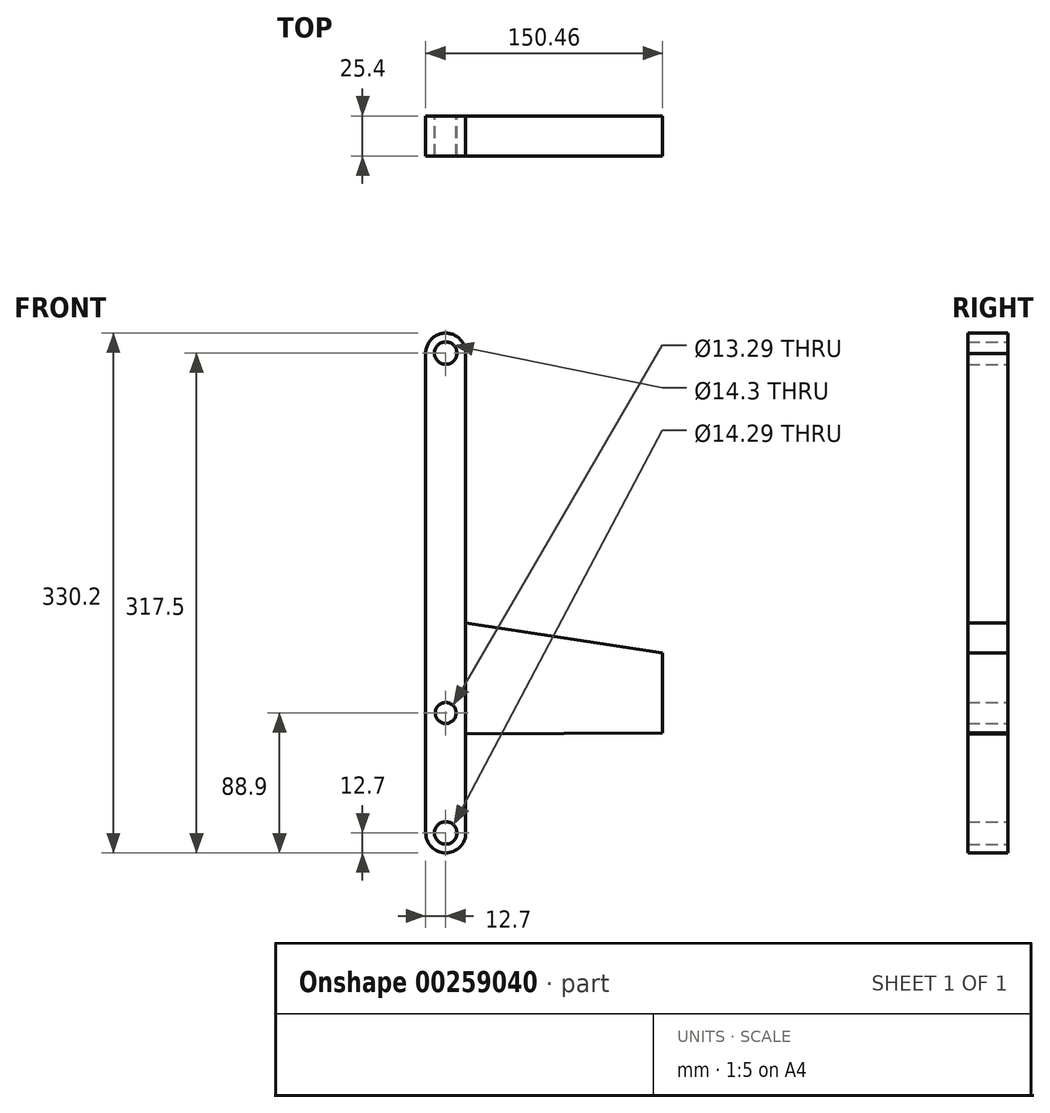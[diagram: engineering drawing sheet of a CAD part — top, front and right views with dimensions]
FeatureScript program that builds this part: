
annotation { "Feature Type Name" : "Feature", "Feature Type Description" : "" }
export const myFeature = defineFeature(function(context is Context, id is Id, definition is map)
    precondition{}
    {
        {
            var Q0;
            Q0=qCreatedBy(makeId("Front.planeOp"),FACE);
            var sketch = newSketch(context, id + "F0", { "sketchPlane" : qUnion([Q0])});
            skCircle(sketch, "E0", {"center": v(0, 0) * mm, "radius": 12.7 * mm});
            skCircle(sketch, "E1", {"center": v(0, 0) * mm, "radius": 7.15 * mm});
            skCircle(sketch, "E2", {"center": v(0, -304.8) * mm, "radius": 12.7 * mm});
            skCircle(sketch, "E3", {"center": v(0, -304.8) * mm, "radius": 7.15 * mm});
            skLineSegment(sketch, "E4", {"start": v(-12.7, 0) * mm, "end": v(-12.7, -304.8) * mm});
            skLineSegment(sketch, "E5", {"start": v(12.7, -0.45) * mm, "end": v(12.7, -304.8) * mm});
            skLineSegment(sketch, "E6.left", {"start": v(12.7, -228.19) * mm, "end": v(12.7, -266.29) * mm});
            skCircle(sketch, "E7", {"center": v(0, -228.6) * mm, "radius": 6.65 * mm});
            skLineSegment(sketch, "E8", {"start": v(12.7, -171.35) * mm, "end": v(137.55, -190.5) * mm});
            skLineSegment(sketch, "E9", {"start": v(137.55, -190.5) * mm, "end": v(137.76, -241.3) * mm});
            skLineSegment(sketch, "E10", {"start": v(137.76, -241.3) * mm, "end": v(12.7, -241.8) * mm});
            skLineSegment(sketch, "E11.MirrorCS", {"start": v(12.7, 0) * mm, "end": v(12.7, -304.8) * mm});
            skSolve(sketch);
        }
        {
            var Q0;
            {var subQ5=sQuery(id+"F0.wireOp",EDGE,"ePRVnAhi-Mh69-9U2p-dATt-yoKc0DpGRvop");Q0=makeQuery(id+"F0.imprint","IMPRINT",FACE,{"disambiguationData":[TD([[makeQuery(id+"F0.imprint","IMPRINT",EDGE,{"derivedFrom":subQ5}),-1.0]])]});}
            var Q1;
            Q1=makeQuery(id+"F0.imprint","IMPRINT",FACE,{"disambiguationData":[TD([[makeQuery(id+"F0.imprint","IMPRINT",EDGE,{"derivedFrom":sQuery(id+"F0.wireOp",EDGE,"E3")}),-1.0]])]});
            var Q2;
            {var subQ4=sQuery(id+"F0.wireOp",EDGE,"E4");Q2=makeQuery(id+"F0.imprint","IMPRINT",FACE,{"disambiguationData":[TD([[makeQuery(id+"F0.imprint","IMPRINT",EDGE,{"derivedFrom":subQ4}),1.0]])]});}
            var Q3;
            Q3=makeQuery(id+"F0.imprint","IMPRINT",FACE,{"disambiguationData":[TD([[makeQuery(id+"F0.imprint","IMPRINT",EDGE,{"derivedFrom":sQuery(id+"F0.wireOp",EDGE,"E1")}),-1.0]])]});
            var Q4;
            {var subQ0=sQuery(id+"F0.wireOp",EDGE,"E8");Q4=makeQuery(id+"F0.imprint","IMPRINT",FACE,{"disambiguationData":[TD([[makeQuery(id+"F0.imprint","IMPRINT",EDGE,{"derivedFrom":subQ0}),-1.0]])]});}
            var Q5;
            {var subQ0=sQuery(id+"F0.wireOp",EDGE,"yVrAon6F-TEJm-yE95-WjNk-o4wYu1XNi6pe");Q5=makeQuery(id+"F0.imprint","IMPRINT",FACE,{"disambiguationData":[TD([[makeQuery(id+"F0.imprint","IMPRINT",EDGE,{"derivedFrom":subQ0}),1.0]])]});}
            var Q6;
            {var subQ0=sQuery(id+"F0.wireOp",EDGE,"w8DVdqsg-hwYO-X7wS-oGyf-7ioYR6odfL98");var subQ1=sQuery(id+"F0.wireOp",EDGE,"o1vL3n55-5nHM-cW2Z-HqQh-5ijmd14oRMik");var subQ2=makeQuery(id+"F0.imprint","INTERSECT",VERTEX,{"derivedFrom":[subQ1,subQ0]});Q6=makeQuery(id+"F0.imprint","IMPRINT",FACE,{"disambiguationData":[TD([[makeQuery(id+"F0.imprint","IMPRINT",EDGE,{"disambiguationData":[TD([[subQ2,-1.0]])],"derivedFrom":subQ1}),-1.0]])]});}
            var Q7;
            Q7=makeQuery(id+"F0.imprint","IMPRINT",FACE,{"disambiguationData":[TD([[makeQuery(id+"F0.imprint","IMPRINT",EDGE,{"derivedFrom":sQuery(id+"F0.wireOp",EDGE,"WU5ookjQ-kl4j-7IFF-bX9O-7W4jz8Cpz3zI")}),-1.0]])]});
            var Q8;
            Q8=makeQuery(id+"F0.imprint","IMPRINT",FACE,{"disambiguationData":[TD([[makeQuery(id+"F0.imprint","IMPRINT",EDGE,{"derivedFrom":sQuery(id+"F0.wireOp",EDGE,"bn22Qj8M-fX78-uC4H-WjcM-HP3O3FltYOQ4")}),-1.0]])]});
            extrude(context, id + "F1", {"entities" : qUnion([Q0, Q1, Q2, Q3, Q4, Q5, Q6, Q7, Q8]), "depth" : 25.4 * mm});
        }
    });
